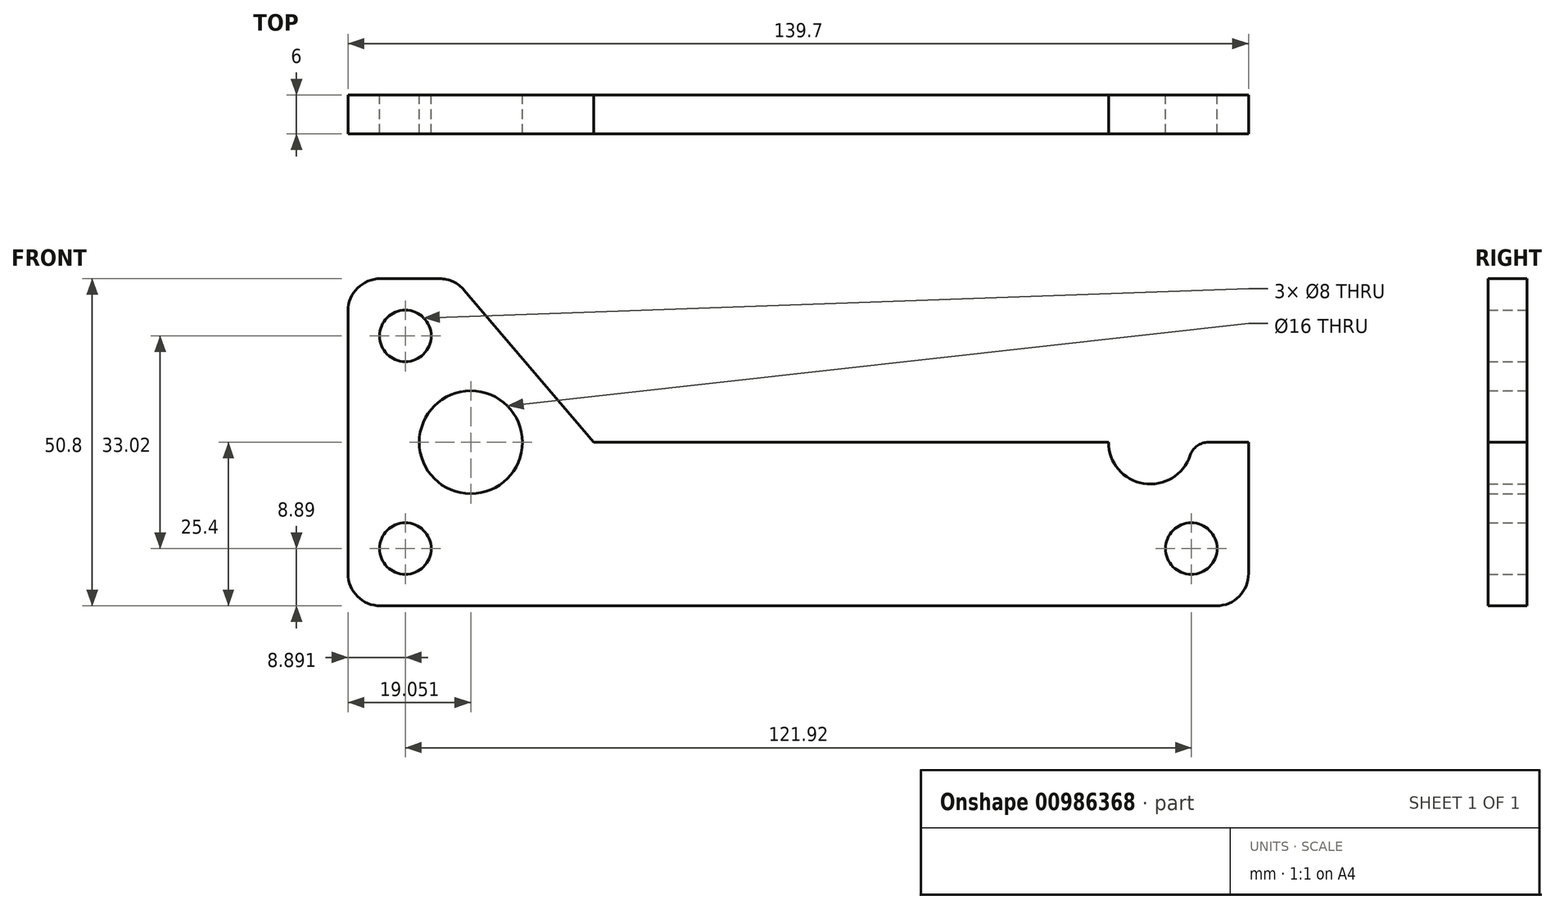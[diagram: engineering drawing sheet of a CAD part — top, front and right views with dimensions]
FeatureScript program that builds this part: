
annotation { "Feature Type Name" : "Feature", "Feature Type Description" : "" }
export const myFeature = defineFeature(function(context is Context, id is Id, definition is map)
    precondition{}
    {
        {
            var Q0;
            Q0=qCreatedBy(makeId("Front.planeOp"),FACE);
            var sketch = newSketch(context, id + "F0", { "sketchPlane" : qUnion([Q0])});
            skLineSegment(sketch, "E0", {"start": v(-67.05, 0) * mm, "end": v(72.65, 0) * mm});
            skLineSegment(sketch, "E1", {"start": v(-67.05, 0) * mm, "end": v(-67.05, 50.8) * mm});
            skLineSegment(sketch, "E2", {"start": v(-67.05, 50.8) * mm, "end": v(-50.54, 50.8) * mm});
            skLineSegment(sketch, "E3", {"start": v(72.65, 0) * mm, "end": v(72.65, 25.4) * mm});
            skLineSegment(sketch, "E4", {"start": v(72.65, 25.4) * mm, "end": v(63.91, 25.4) * mm});
            skLineSegment(sketch, "E5", {"start": v(-28.95, 25.4) * mm, "end": v(-50.54, 50.8) * mm});
            skArc(sketch, "E6", {"start": v(50.91, 25.4) * mm, "mid": v(57.41, 18.9) * mm, "end": v(63.91, 25.4) * mm});
            skLineSegment(sketch, "E7.trimOffspring", {"start": v(50.91, 25.4) * mm, "end": v(-28.95, 25.4) * mm});
            skPoint(sketch, "E8.end.orphan", {"position": v(61.33, 8.89) * mm});
            skCircle(sketch, "E9", {"center": v(63.76, 8.89) * mm, "radius": 4 * mm});
            skPoint(sketch, "E10.orphan", {"position": v(72.65, 8.89) * mm});
            skLineSegment(sketch, "E11", {"start": v(-67.05, 0) * mm, "end": v(-67.05, 8.9) * mm});
            skCircle(sketch, "E12", {"center": v(-58.16, 8.9) * mm, "radius": 4 * mm});
            skLineSegment(sketch, "E13", {"start": v(-67.05, 50.8) * mm, "end": v(-67.05, 41.9) * mm});
            skCircle(sketch, "E14", {"center": v(-58.16, 41.9) * mm, "radius": 4 * mm});
            skCircle(sketch, "E15", {"center": v(-48, 25.4) * mm, "radius": 8 * mm});
            skPoint(sketch, "E16.orphan", {"position": v(-67.05, 25.4) * mm});
            skSolve(sketch);
        }
        {
            var Q0;
            Q0 = qSketchRegion(id + "F0", true);
            extrude(context, id + "F1", {"entities" : qUnion([Q0]), "depth" : 6 * mm, "offsetDistance" : 25 * mm});
        }
        {
            var Q0;
            Q0=makeQuery(id+"F1.opExtrude","SWEPT_EDGE",EDGE,{"disambiguationData":[OSD([sQuery(id+"F0.wireOp",EDGE,"E2"),sQuery(id+"F0.wireOp",EDGE,"E13")])]});
            var Q1;
            Q1=makeQuery(id+"F1.opExtrude","SWEPT_EDGE",EDGE,{"disambiguationData":[OSD([sQuery(id+"F0.wireOp",EDGE,"E0"),sQuery(id+"F0.wireOp",EDGE,"E11")])]});
            var Q2;
            Q2=makeQuery(id+"F1.opExtrude","SWEPT_EDGE",EDGE,{"disambiguationData":[OSD([sQuery(id+"F0.wireOp",EDGE,"E0"),sQuery(id+"F0.wireOp",EDGE,"E3")])]});
            fillet(context, id + "F2", {"entities" : qUnion([Q0, Q1, Q2]), "radius" : 5 * mm, "tangentPropagation" : true, "allowEdgeOverflow" : false});
        }
        {
            var Q0;
            Q0=makeQuery(id+"F1.opExtrude","SWEPT_EDGE",EDGE,{"disambiguationData":[OSD([sQuery(id+"F0.wireOp",EDGE,"E4"),sQuery(id+"F0.wireOp",EDGE,"E6")])]});
            fillet(context, id + "F3", {"entities" : qUnion([Q0]), "radius" : 3 * mm, "tangentPropagation" : true, "allowEdgeOverflow" : false});
        }
    });
